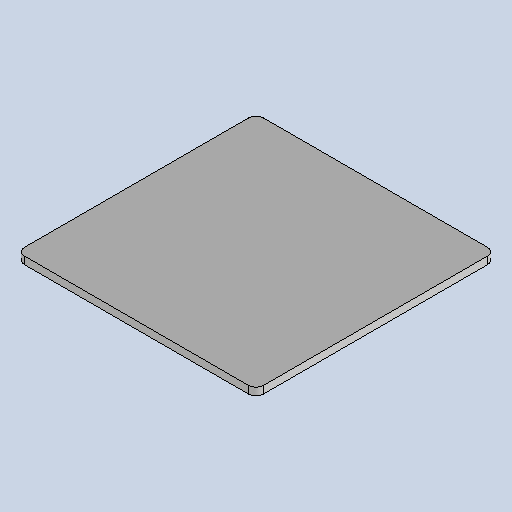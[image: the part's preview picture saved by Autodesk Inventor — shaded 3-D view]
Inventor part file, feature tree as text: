
AUTODESK INVENTOR PART (.ipt)
format: ipt  version: 2025.3 (Build 293356030, 356C)  size: 193,536 bytes
history: native  units: mm
features: sheet_metal_op x4, other x4, sketch x3, chamfer x2, projected_geometry x1
ambient origin geometry x8: Origin, YZ Plane, XZ Plane, XY Plane, X Axis, Y Axis, Z Axis, Center Point
bodies: Body1 (feature_tree)
feature tree (14):
  sheet_metal_op  "Face3"
  chamfer  "Corner Round1"
  sheet_metal_op  "Flange4"
  chamfer  "Corner Round3"
  sketch  "Sketch1"  dims[d154=64.0mm]
  other  "Plate5"
  sketch  "Sketch10"  dims[d155=64.0mm]
  other  "Plate7"
  sheet_metal_op  "Bend4"
  sheet_metal_op  "Corner4"
  sketch  "Sketch11"  dims[d156=2.0mm d178=2.0mm d180=2.0mm d181=1.0mm d182=4.0mm d183=2.75mm d184=30.0mm d185=90.0deg d186=2.75mm d187=20.0mm d188=20.0mm d189=8.0mm d190=2.0mm d191=2.75mm d192=11.0mm d193=10.0mm d194=2.0mm d195=0.0mm d196=6.0mm]
  projected_geometry  "Projected Loop3"
  other  "Cut3"
  other  "Definition1"
